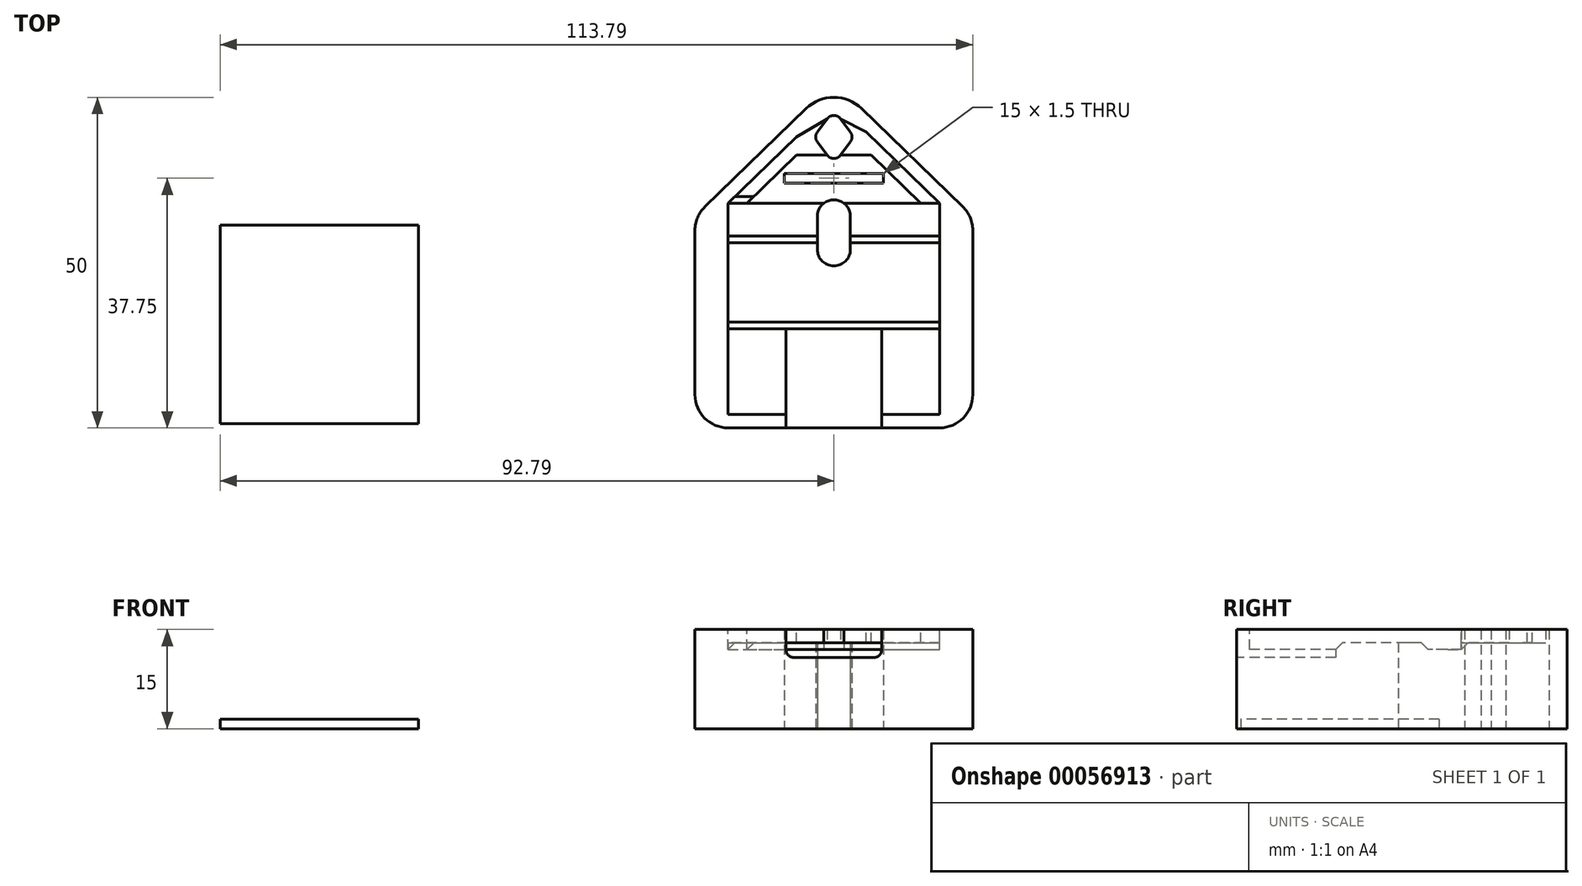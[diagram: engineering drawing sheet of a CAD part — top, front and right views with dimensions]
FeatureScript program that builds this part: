
annotation { "Feature Type Name" : "Feature", "Feature Type Description" : "" }
export const myFeature = defineFeature(function(context is Context, id is Id, definition is map)
    precondition{}
    {
        {
            var Q0;
            Q0=qCreatedBy(makeId("Top.planeOp"),FACE);
            var sketch = newSketch(context, id + "F0", { "sketchPlane" : qUnion([Q0])});
            skLineSegment(sketch, "E0.bottom", {"start": v(-92.79, 6.65) * mm, "end": v(-62.79, 6.65) * mm});
            skLineSegment(sketch, "E0.top", {"start": v(-92.79, -23.35) * mm, "end": v(-62.79, -23.35) * mm});
            skLineSegment(sketch, "E0.left", {"start": v(-92.79, 6.65) * mm, "end": v(-92.79, -23.35) * mm});
            skLineSegment(sketch, "E0.right", {"start": v(-62.79, 6.65) * mm, "end": v(-62.79, -23.35) * mm});
            skSolve(sketch);
        }
        {
            var Q0;
            Q0=makeQuery(id+"F0.imprint","IMPRINT",FACE,{"disambiguationData":[TD([[makeQuery(id+"F0.imprint","IMPRINT",EDGE,{"derivedFrom":sQuery(id+"F0.wireOp",EDGE,"E0.bottom")}),-1.0]])]});
            extrude(context, id + "F1", {"entities" : qUnion([Q0]), "depth" : 1.4 * mm});
        }
        {
            var Q0;
            Q0=qCreatedBy(makeId("Top.planeOp"),FACE);
            var sketch = newSketch(context, id + "F2", { "sketchPlane" : qUnion([Q0])});
            skArc(sketch, "E1", {"start": v(4.18, 24.3) * mm, "mid": v(0, 26) * mm, "end": v(-4.18, 24.3) * mm});
            skLineSegment(sketch, "E2.top", {"start": v(-16, -24) * mm, "end": v(16, -24) * mm});
            skLineSegment(sketch, "E2.left", {"start": v(-21, 5.88) * mm, "end": v(-21, -19) * mm});
            skLineSegment(sketch, "E2.right", {"start": v(21, 5.88) * mm, "end": v(21, -19) * mm});
            skLineSegment(sketch, "E3", {"start": v(-19.48, 9.47) * mm, "end": v(-4.18, 24.3) * mm});
            skLineSegment(sketch, "E4", {"start": v(19.48, 9.47) * mm, "end": v(4.18, 24.3) * mm});
            skArc(sketch, "E5", {"start": v(1, 22.75) * mm, "mid": v(0, 23.25) * mm, "end": v(-1, 22.75) * mm});
            skArc(sketch, "E6", {"start": v(-1, 17.25) * mm, "mid": v(0, 16.75) * mm, "end": v(1, 17.25) * mm});
            skArc(sketch, "E7", {"start": v(2.5, 19.25) * mm, "mid": v(2.75, 20) * mm, "end": v(2.5, 20.75) * mm});
            skArc(sketch, "E8", {"start": v(-2.5, 20.75) * mm, "mid": v(-2.75, 20) * mm, "end": v(-2.5, 19.25) * mm});
            skLineSegment(sketch, "E9", {"start": v(-2.5, 20.75) * mm, "end": v(-1, 22.75) * mm});
            skLineSegment(sketch, "E10", {"start": v(1, 22.75) * mm, "end": v(2.5, 20.75) * mm});
            skLineSegment(sketch, "E11", {"start": v(2.5, 19.25) * mm, "end": v(1, 17.25) * mm});
            skLineSegment(sketch, "E12", {"start": v(-1, 17.25) * mm, "end": v(-2.5, 19.25) * mm});
            skLineSegment(sketch, "E13.bottom", {"start": v(-7.5, 14.5) * mm, "end": v(7.5, 14.5) * mm});
            skLineSegment(sketch, "E13.top", {"start": v(-7.5, 13) * mm, "end": v(7.5, 13) * mm});
            skLineSegment(sketch, "E13.left", {"start": v(-7.5, 14.5) * mm, "end": v(-7.5, 13) * mm});
            skLineSegment(sketch, "E13.right", {"start": v(7.5, 14.5) * mm, "end": v(7.5, 13) * mm});
            skArc(sketch, "E14", {"start": v(2.5, 8) * mm, "mid": v(0, 10.5) * mm, "end": v(-2.5, 8) * mm});
            skArc(sketch, "E15", {"start": v(-2.5, 3) * mm, "mid": v(0, 0.5) * mm, "end": v(2.5, 3) * mm});
            skLineSegment(sketch, "E16", {"start": v(2.5, 8) * mm, "end": v(2.5, 3) * mm});
            skLineSegment(sketch, "E17", {"start": v(-2.5, 3) * mm, "end": v(-2.5, 8) * mm});
            skPoint(sketch, "E18.visualSharp", {"position": v(-21, -24) * mm});
            skArc(sketch, "E18.filletArc", {"start": v(-21, -19) * mm, "mid": v(-19.54, -22.54) * mm, "end": v(-16, -24) * mm});
            skPoint(sketch, "E19.visualSharp", {"position": v(21, -24) * mm});
            skArc(sketch, "E19.filletArc", {"start": v(16, -24) * mm, "mid": v(19.54, -22.54) * mm, "end": v(21, -19) * mm});
            skPoint(sketch, "E20.visualSharp", {"position": v(21, 8) * mm});
            skArc(sketch, "E20.filletArc", {"start": v(21, 5.88) * mm, "mid": v(20.6, 7.83) * mm, "end": v(19.48, 9.47) * mm});
            skPoint(sketch, "E21.visualSharp", {"position": v(-21, 8) * mm});
            skArc(sketch, "E21.filletArc", {"start": v(-19.48, 9.47) * mm, "mid": v(-20.6, 7.83) * mm, "end": v(-21, 5.88) * mm});
            skSolve(sketch);
        }
        {
            var Q0;
            Q0 = qSketchRegion(id + "F2", true);
            extrude(context, id + "F3", {"entities" : qUnion([Q0]), "depth" : 15 * mm});
        }
        {
            var Q0;
            Q0=makeQuery(id+"F3.opExtrude","CAP_FACE",FACE,{"disambiguationData":[OSD([sQuery(id+"F2.wireOp",EDGE,"E1"),sQuery(id+"F2.wireOp",EDGE,"E2.top"),sQuery(id+"F2.wireOp",EDGE,"E2.left"),sQuery(id+"F2.wireOp",EDGE,"E2.right"),sQuery(id+"F2.wireOp",EDGE,"E3"),sQuery(id+"F2.wireOp",EDGE,"E4"),sQuery(id+"F2.wireOp",EDGE,"E5"),sQuery(id+"F2.wireOp",EDGE,"E6"),sQuery(id+"F2.wireOp",EDGE,"E7"),sQuery(id+"F2.wireOp",EDGE,"E8"),sQuery(id+"F2.wireOp",EDGE,"E9"),sQuery(id+"F2.wireOp",EDGE,"E10"),sQuery(id+"F2.wireOp",EDGE,"E11"),sQuery(id+"F2.wireOp",EDGE,"E12"),sQuery(id+"F2.wireOp",EDGE,"E13.bottom"),sQuery(id+"F2.wireOp",EDGE,"E13.top"),sQuery(id+"F2.wireOp",EDGE,"E13.left"),sQuery(id+"F2.wireOp",EDGE,"E13.right"),sQuery(id+"F2.wireOp",EDGE,"E14"),sQuery(id+"F2.wireOp",EDGE,"E15"),sQuery(id+"F2.wireOp",EDGE,"E16"),sQuery(id+"F2.wireOp",EDGE,"E17"),sQuery(id+"F2.wireOp",EDGE,"E18.filletArc"),sQuery(id+"F2.wireOp",EDGE,"E19.filletArc"),sQuery(id+"F2.wireOp",EDGE,"E20.filletArc"),sQuery(id+"F2.wireOp",EDGE,"E21.filletArc")])],"isStart":false});
            var sketch = newSketch(context, id + "F4", { "sketchPlane" : qUnion([Q0])});
            skLineSegment(sketch, "E22.bottom", {"start": v(-13.13, 10) * mm, "end": v(13.13, 10) * mm});
            skLineSegment(sketch, "E22.top", {"start": v(-16, -22) * mm, "end": v(16, -22) * mm});
            skLineSegment(sketch, "E22.left", {"start": v(-16, 10) * mm, "end": v(-16, -22) * mm});
            skLineSegment(sketch, "E22.right", {"start": v(16, 10) * mm, "end": v(16, -22) * mm});
            skLineSegment(sketch, "E23", {"start": v(-16, 10) * mm, "end": v(-5.68, 20) * mm});
            skPoint(sketch, "E23.endSnap0", {"position": v(-2.75, 20) * mm});
            skLineSegment(sketch, "E24", {"start": v(-5.68, 20) * mm, "end": v(-1, 22.75) * mm});
            skLineSegment(sketch, "E25", {"start": v(-13.13, 10) * mm, "end": v(-5.65, 17.25) * mm});
            skLineSegment(sketch, "E26", {"start": v(-5.65, 17.25) * mm, "end": v(-1, 17.25) * mm});
            skLineSegment(sketch, "E27", {"start": v(-1, 17.25) * mm, "end": v(-1, 22.75) * mm});
            skLineSegment(sketch, "E28", {"start": v(16, 10) * mm, "end": v(4.91, 20.75) * mm});
            skLineSegment(sketch, "E29", {"start": v(4.91, 20.75) * mm, "end": v(1, 22.75) * mm});
            skLineSegment(sketch, "E30", {"start": v(1, 22.75) * mm, "end": v(1, 17.25) * mm});
            skLineSegment(sketch, "E31", {"start": v(1, 17.25) * mm, "end": v(5.65, 17.25) * mm});
            skLineSegment(sketch, "E32", {"start": v(5.65, 17.25) * mm, "end": v(13.13, 10) * mm});
            skSolve(sketch);
        }
        {
            var Q0;
            Q0 = qSketchRegion(id + "F4", true);
            extrude(context, id + "F5", {"entities" : qUnion([Q0]), "operationType" : NewBodyOperationType.REMOVE, "oppositeDirection" : true, "depth" : 2 * mm});
        }
        {
            var Q0;
            Q0=makeQuery(id+"F3.opExtrude","SWEPT_FACE",FACE,{"disambiguationData":[OSD([sQuery(id+"F2.wireOp",EDGE,"E2.top")])]});
            var sketch = newSketch(context, id + "F6", { "sketchPlane" : qUnion([Q0])});
            skArc(sketch, "E33", {"start": v(-7.25, 12) * mm, "mid": v(-6.88, 11.12) * mm, "end": v(-6, 10.75) * mm});
            skArc(sketch, "E34", {"start": v(6, 10.75) * mm, "mid": v(6.88, 11.12) * mm, "end": v(7.25, 12) * mm});
            skLineSegment(sketch, "E35", {"start": v(-7.25, 12) * mm, "end": v(-7.25, 15) * mm});
            skPoint(sketch, "E35.endSnap0", {"position": v(0, 15) * mm});
            skLineSegment(sketch, "E36", {"start": v(-7.25, 15) * mm, "end": v(7.25, 15) * mm});
            skLineSegment(sketch, "E37", {"start": v(7.25, 15) * mm, "end": v(7.25, 12) * mm});
            skLineSegment(sketch, "E38", {"start": v(-6, 10.75) * mm, "end": v(6, 10.75) * mm});
            skSolve(sketch);
        }
        {
            var Q0;
            Q0 = qSketchRegion(id + "F6", true);
            extrude(context, id + "F7", {"entities" : qUnion([Q0]), "operationType" : NewBodyOperationType.REMOVE, "oppositeDirection" : true, "depth" : 15 * mm});
        }
        {
            var Q0;
            Q0=makeQuery(id+"F5.boolean.opBoolean","COPY",FACE,{"derivedFrom":makeQuery(id+"F5.opExtrude","CAP_FACE",FACE,{"disambiguationData":[OSD([sQuery(id+"F4.wireOp",EDGE,"E22.bottom"),sQuery(id+"F4.wireOp",EDGE,"E22.top"),sQuery(id+"F4.wireOp",EDGE,"E22.left"),sQuery(id+"F4.wireOp",EDGE,"E22.right"),sQuery(id+"F4.wireOp",EDGE,"E23"),sQuery(id+"F4.wireOp",EDGE,"E24"),sQuery(id+"F4.wireOp",EDGE,"E25"),sQuery(id+"F4.wireOp",EDGE,"E26"),sQuery(id+"F4.wireOp",EDGE,"E27"),sQuery(id+"F4.wireOp",EDGE,"E28"),sQuery(id+"F4.wireOp",EDGE,"E29"),sQuery(id+"F4.wireOp",EDGE,"E30"),sQuery(id+"F4.wireOp",EDGE,"E31"),sQuery(id+"F4.wireOp",EDGE,"E32")])],"isStart":false})});
            var sketch = newSketch(context, id + "F8", { "sketchPlane" : qUnion([Q0])});
            skLineSegment(sketch, "E39.bottom", {"start": v(-16, 10) * mm, "end": v(16, 10) * mm});
            skLineSegment(sketch, "E39.top", {"start": v(-16, 5) * mm, "end": v(16, 5) * mm});
            skLineSegment(sketch, "E39.left", {"start": v(-16, 10) * mm, "end": v(-16, 5) * mm});
            skLineSegment(sketch, "E39.right", {"start": v(16, 10) * mm, "end": v(16, 5) * mm});
            skLineSegment(sketch, "E40.bottom", {"start": v(-16, -22) * mm, "end": v(16, -22) * mm});
            skLineSegment(sketch, "E40.top", {"start": v(-16, -9) * mm, "end": v(16, -9) * mm});
            skLineSegment(sketch, "E40.left", {"start": v(-16, -22) * mm, "end": v(-16, -9) * mm});
            skLineSegment(sketch, "E40.right", {"start": v(16, -22) * mm, "end": v(16, -9) * mm});
            skSolve(sketch);
        }
        {
            var Q0;
            Q0 = qSketchRegion(id + "F8", true);
            extrude(context, id + "F9", {"entities" : qUnion([Q0]), "operationType" : NewBodyOperationType.REMOVE, "oppositeDirection" : true, "depth" : 1 * mm});
        }
        {
            var Q0;
            Q0=makeQuery(id+"F9.boolean.opBoolean","COPY",EDGE,{"disambiguationData":[OD(1.0)],"derivedFrom":makeQuery(id+"F9.opExtrude","CAP_EDGE",EDGE,{"disambiguationData":[OSD([sQuery(id+"F8.wireOp",EDGE,"E39.bottom")])],"isStart":true})});
            var Q1;
            Q1=makeQuery(id+"F9.boolean.opBoolean","COPY",EDGE,{"disambiguationData":[OD(0.0)],"derivedFrom":makeQuery(id+"F9.opExtrude","CAP_EDGE",EDGE,{"disambiguationData":[OSD([sQuery(id+"F8.wireOp",EDGE,"E39.bottom")])],"isStart":true})});
            var Q2;
            Q2=makeQuery(id+"F9.boolean.opBoolean","COPY",EDGE,{"disambiguationData":[OD(1.0)],"derivedFrom":makeQuery(id+"F9.opExtrude","CAP_EDGE",EDGE,{"disambiguationData":[OSD([sQuery(id+"F8.wireOp",EDGE,"E39.top")])],"isStart":true})});
            var Q3;
            Q3=makeQuery(id+"F9.boolean.opBoolean","COPY",EDGE,{"disambiguationData":[OD(0.0)],"derivedFrom":makeQuery(id+"F9.opExtrude","CAP_EDGE",EDGE,{"disambiguationData":[OSD([sQuery(id+"F8.wireOp",EDGE,"E39.top")])],"isStart":true})});
            var Q4;
            Q4=makeQuery(id+"F9.boolean.opBoolean","MERGE",EDGE,{"derivedFrom":[makeQuery(id+"F7.boolean.opBoolean","INTERSECT",EDGE,{"derivedFrom":[makeQuery(id+"F5.boolean.opBoolean","COPY",FACE,{"derivedFrom":makeQuery(id+"F5.opExtrude","CAP_FACE",FACE,{"disambiguationData":[OSD([sQuery(id+"F4.wireOp",EDGE,"E22.bottom"),sQuery(id+"F4.wireOp",EDGE,"E22.top"),sQuery(id+"F4.wireOp",EDGE,"E22.left"),sQuery(id+"F4.wireOp",EDGE,"E22.right"),sQuery(id+"F4.wireOp",EDGE,"E23"),sQuery(id+"F4.wireOp",EDGE,"E24"),sQuery(id+"F4.wireOp",EDGE,"E25"),sQuery(id+"F4.wireOp",EDGE,"E26"),sQuery(id+"F4.wireOp",EDGE,"E27"),sQuery(id+"F4.wireOp",EDGE,"E28"),sQuery(id+"F4.wireOp",EDGE,"E29"),sQuery(id+"F4.wireOp",EDGE,"E30"),sQuery(id+"F4.wireOp",EDGE,"E31"),sQuery(id+"F4.wireOp",EDGE,"E32")])],"isStart":false})}),makeQuery(id+"F7.opExtrude","CAP_FACE",FACE,{"disambiguationData":[OSD([sQuery(id+"F6.wireOp",EDGE,"E33"),sQuery(id+"F6.wireOp",EDGE,"E34"),sQuery(id+"F6.wireOp",EDGE,"E35"),sQuery(id+"F6.wireOp",EDGE,"E36"),sQuery(id+"F6.wireOp",EDGE,"E37"),sQuery(id+"F6.wireOp",EDGE,"E38")])],"isStart":false})]}),makeQuery(id+"F9.opExtrude","CAP_EDGE",EDGE,{"disambiguationData":[OSD([sQuery(id+"F8.wireOp",EDGE,"E40.top")])],"isStart":true})]});
            chamfer(context, id + "F10", {"entities" : qUnion([Q0, Q1, Q2, Q3, Q4]), "width" : 1 * mm, "tangentPropagation" : true});
        }
    });
